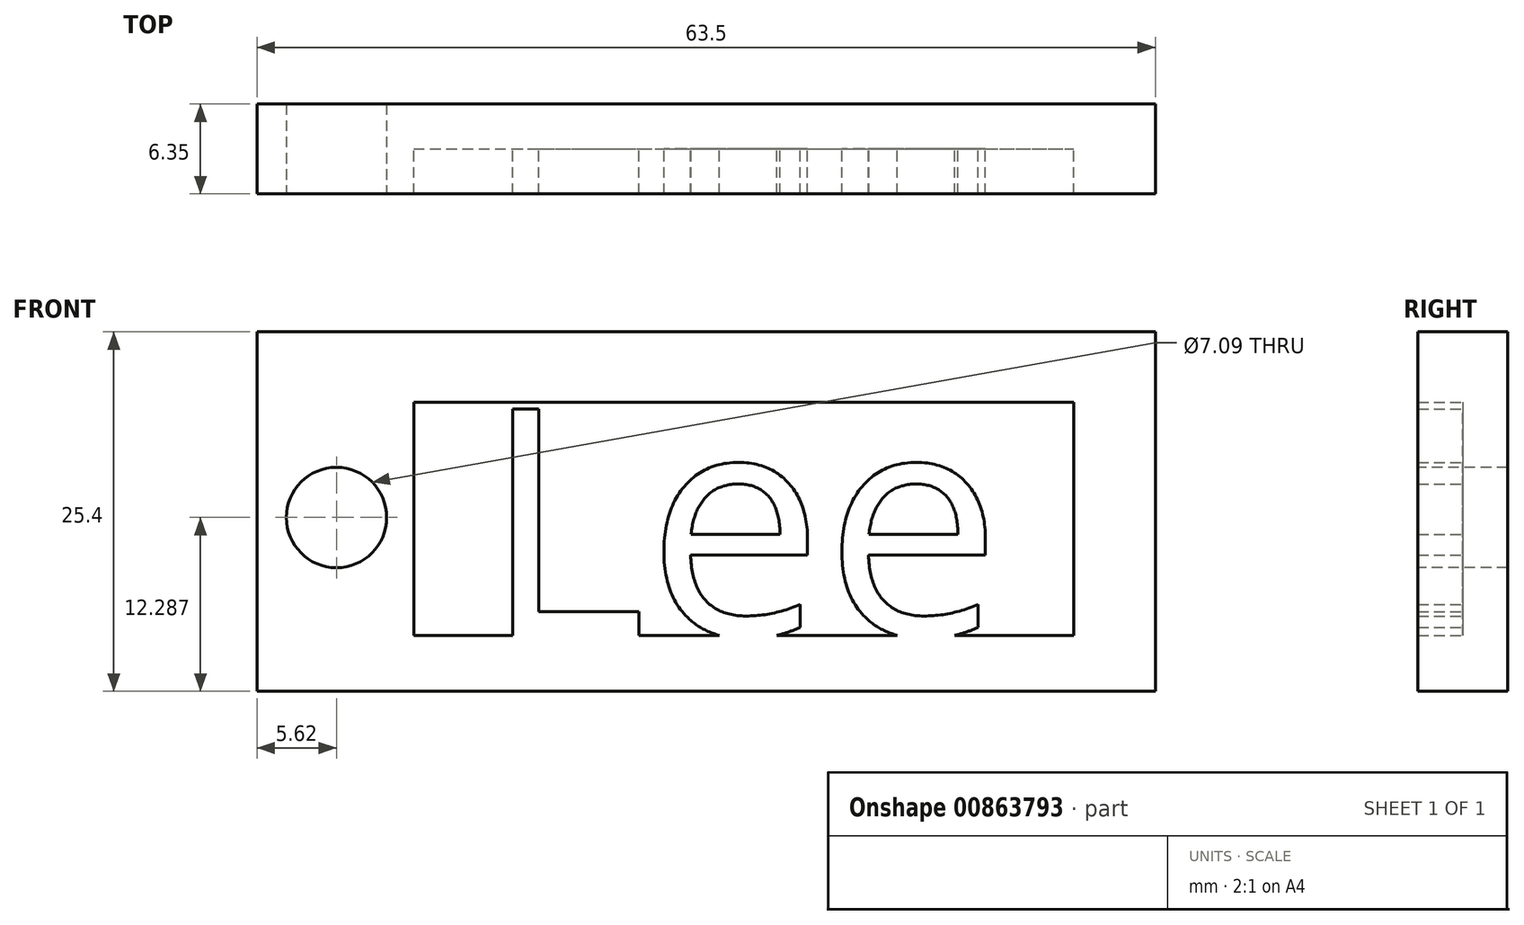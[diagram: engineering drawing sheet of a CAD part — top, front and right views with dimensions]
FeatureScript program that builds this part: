
annotation { "Feature Type Name" : "Feature", "Feature Type Description" : "" }
export const myFeature = defineFeature(function(context is Context, id is Id, definition is map)
    precondition{}
    {
        {
            var Q0;
            Q0=qCreatedBy(makeId("Front.planeOp"),FACE);
            var sketch = newSketch(context, id + "F0", { "sketchPlane" : qUnion([Q0])});
            skLineSegment(sketch, "E0.bottom", {"start": v(0, 25.4) * mm, "end": v(63.5, 25.4) * mm});
            skLineSegment(sketch, "E0.top", {"start": v(0, 0) * mm, "end": v(63.5, 0) * mm});
            skLineSegment(sketch, "E0.left", {"start": v(0, 25.4) * mm, "end": v(0, 0) * mm});
            skLineSegment(sketch, "E0.right", {"start": v(63.5, 25.4) * mm, "end": v(63.5, 0) * mm});
            skLineSegment(sketch, "E1.bottom", {"start": v(11.08, 20.43) * mm, "end": v(57.73, 20.43) * mm});
            skLineSegment(sketch, "E1.top", {"start": v(11.08, 3.96) * mm, "end": v(57.73, 3.96) * mm});
            skLineSegment(sketch, "E1.left", {"start": v(11.08, 20.43) * mm, "end": v(11.08, 3.96) * mm});
            skLineSegment(sketch, "E1.right", {"start": v(57.73, 20.43) * mm, "end": v(57.73, 3.96) * mm});
            skSolve(sketch);
        }
        {
            var Q0;
            Q0 = qSketchRegion(id + "F0", true);
            extrude(context, id + "F1", {"entities" : qUnion([Q0]), "depth" : 6.35 * mm, "offsetDistance" : 25.4 * mm});
        }
        {
            var Q0;
            Q0=makeQuery(id+"F0.imprint","IMPRINT",FACE,{"disambiguationData":[TD([[makeQuery(id+"F0.imprint","IMPRINT",EDGE,{"derivedFrom":sQuery(id+"F0.wireOp",EDGE,"E1.bottom")}),-1.0]])]});
            extrude(context, id + "F2", {"entities" : qUnion([Q0]), "operationType" : NewBodyOperationType.ADD, "depth" : 3.17 * mm, "offsetDistance" : 25.4 * mm});
        }
        {
            var Q0;
            Q0=makeQuery(id+"F1.opExtrude","CAP_FACE",FACE,{"disambiguationData":[OSD([sQuery(id+"F0.wireOp",EDGE,"E0.bottom"),sQuery(id+"F0.wireOp",EDGE,"E0.top"),sQuery(id+"F0.wireOp",EDGE,"E0.left"),sQuery(id+"F0.wireOp",EDGE,"E0.right"),sQuery(id+"F0.wireOp",EDGE,"E1.bottom"),sQuery(id+"F0.wireOp",EDGE,"E1.top"),sQuery(id+"F0.wireOp",EDGE,"E1.left"),sQuery(id+"F0.wireOp",EDGE,"E1.right")])],"isStart":false});
            var sketch = newSketch(context, id + "F3", { "sketchPlane" : qUnion([Q0])});
            skCircle(sketch, "E2", {"center": v(5.62, 12.29) * mm, "radius": 3.55 * mm});
            skSolve(sketch);
        }
        {
            var Q0;
            Q0 = qSketchRegion(id + "F3", true);
            extrude(context, id + "F4", {"entities" : qUnion([Q0]), "operationType" : NewBodyOperationType.REMOVE, "oppositeDirection" : true, "depth" : 25.4 * mm, "offsetDistance" : 25.4 * mm});
        }
        {
            var Q0;
            Q0=makeQuery(id+"F2.opExtrude","CAP_FACE",FACE,{"disambiguationData":[OSD([sQuery(id+"F0.wireOp",EDGE,"E1.bottom"),sQuery(id+"F0.wireOp",EDGE,"E1.top"),sQuery(id+"F0.wireOp",EDGE,"E1.left"),sQuery(id+"F0.wireOp",EDGE,"E1.right")])],"isStart":false});
            var sketch = newSketch(context, id + "F5", { "sketchPlane" : qUnion([Q0])});
            skText(sketch, "E3", { "text": "Lee", "fontName": "OpenSans-Regular.ttf"});
            skPoint(sketch, "E4", {"position": v(34.4, 20.43) * mm});
            const initialGuessF5  = {"E3": [0.01587, 0.00396, 1, 0, 0.01614]};
            skSetInitialGuess(sketch, initialGuessF5);
            skSolve(sketch);
        }
        {
            var Q0;
            Q0 = qSketchRegion(id + "F5", true);
            extrude(context, id + "F6", {"entities" : qUnion([Q0]), "operationType" : NewBodyOperationType.ADD, "depth" : 3.17 * mm, "offsetDistance" : 25.4 * mm});
        }
    });
